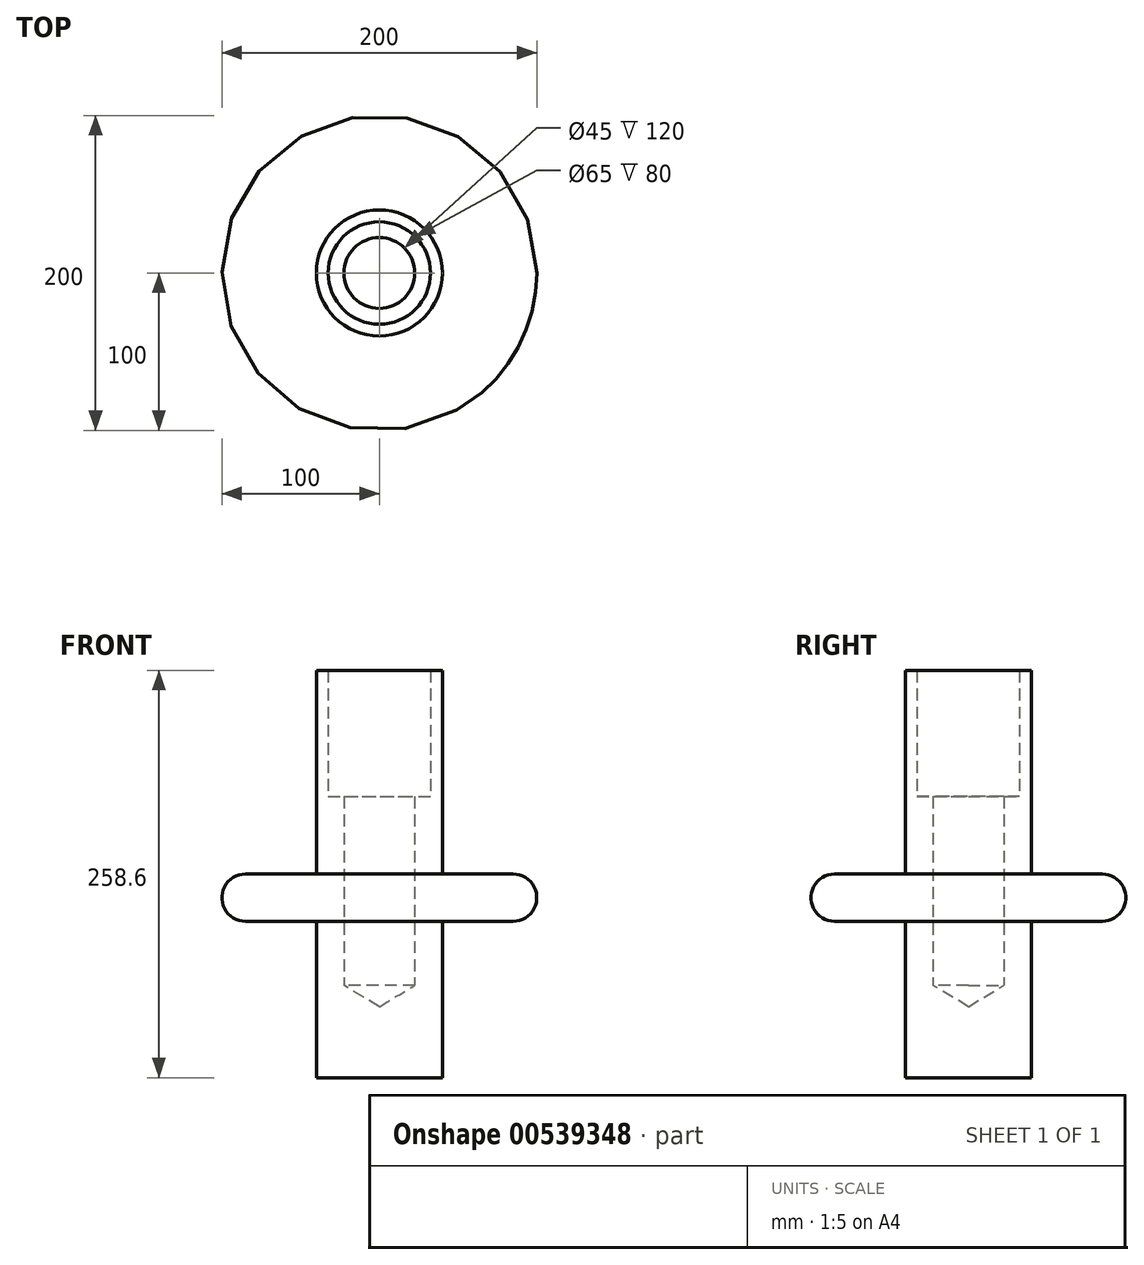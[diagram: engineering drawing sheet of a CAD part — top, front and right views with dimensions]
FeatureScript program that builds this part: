
annotation { "Feature Type Name" : "Feature", "Feature Type Description" : "" }
export const myFeature = defineFeature(function(context is Context, id is Id, definition is map)
    precondition{}
    {
        {
            var Q0;
            Q0=qCreatedBy(makeId("Top.planeOp"),FACE);
            var sketch = newSketch(context, id + "F0", { "sketchPlane" : qUnion([Q0])});
            skCircle(sketch, "E0", {"center": v(0, 0) * mm, "radius": 100 * mm});
            skSolve(sketch);
        }
        {
            var Q0;
            Q0 = qSketchRegion(id + "F0", true);
            extrude(context, id + "F1", {"entities" : qUnion([Q0]), "depth" : 30 * mm, "offsetDistance" : 25 * mm});
        }
        {
            var Q0;
            Q0=makeQuery(id+"F1.opExtrude","CAP_FACE",FACE,{"disambiguationData":[OSD([sQuery(id+"F0.wireOp",EDGE,"E0")])],"isStart":false});
            var sketch = newSketch(context, id + "F2", { "sketchPlane" : qUnion([Q0])});
            skCircle(sketch, "E1", {"center": v(0, 0) * mm, "radius": 40 * mm});
            skSolve(sketch);
        }
        {
            var Q0;
            Q0 = qSketchRegion(id + "F2", true);
            extrude(context, id + "F3", {"entities" : qUnion([Q0]), "operationType" : NewBodyOperationType.ADD, "depth" : 258.6 * mm, "offsetDistance" : 25 * mm, "symmetric" : true});
        }
        {
            var Q0;
            Q0=makeQuery(id+"F1.opExtrude","CAP_EDGE",EDGE,{"disambiguationData":[OSD([sQuery(id+"F0.wireOp",EDGE,"E0")])],"isStart":false});
            var Q1;
            Q1=makeQuery(id+"F1.opExtrude","SWEPT_FACE",FACE,{"disambiguationData":[OSD([sQuery(id+"F0.wireOp",EDGE,"E0")])]});
            fillet(context, id + "F4", {"entities" : qUnion([Q0, Q1]), "radius" : 15 * mm, "tangentPropagation" : true, "allowEdgeOverflow" : false});
        }
        {
            var Q0;
            Q0=makeQuery(id+"F3.opExtrude","CAP_FACE",FACE,{"disambiguationData":[OSD([sQuery(id+"F2.wireOp",EDGE,"E1")])],"isStart":false});
            var sketch = newSketch(context, id + "F5", { "sketchPlane" : qUnion([Q0])});
            skPoint(sketch, "E2", {"position": v(0, 0) * mm});
            skPoint(sketch, "E3", {"position": v(-104.76, -38.92) * mm});
            skSolve(sketch);
        }
        {
            var Q0;
            Q0=sQuery(id+"F5.wireOp",VERTEX,"E2");
            var Q1;
            Q1=makeQuery(id+"F1.opExtrude","SWEPT_BODY",BODY,{"disambiguationData":[OSD([sQuery(id+"F0.wireOp",EDGE,"E0")])]});
            hole(context, id + "F6", {"style" : HoleStyle.C_BORE, "endStyle" : HoleEndStyle.BLIND, "holeDiameter" : 45 * mm, "cBoreDiameter" : 65 * mm, "cBoreDepth" : 80 * mm, "majorDiameter" : 5 * mm, "holeDepth" : 200 * mm, "isTappedThrough" : true, "tappedDepth" : 12 * mm, "tapClearance" : 3, "locations" : qUnion([Q0]), "scope" : qUnion([Q1]), "startStyle" : HoleStartStyle.PART});
        }
    });
